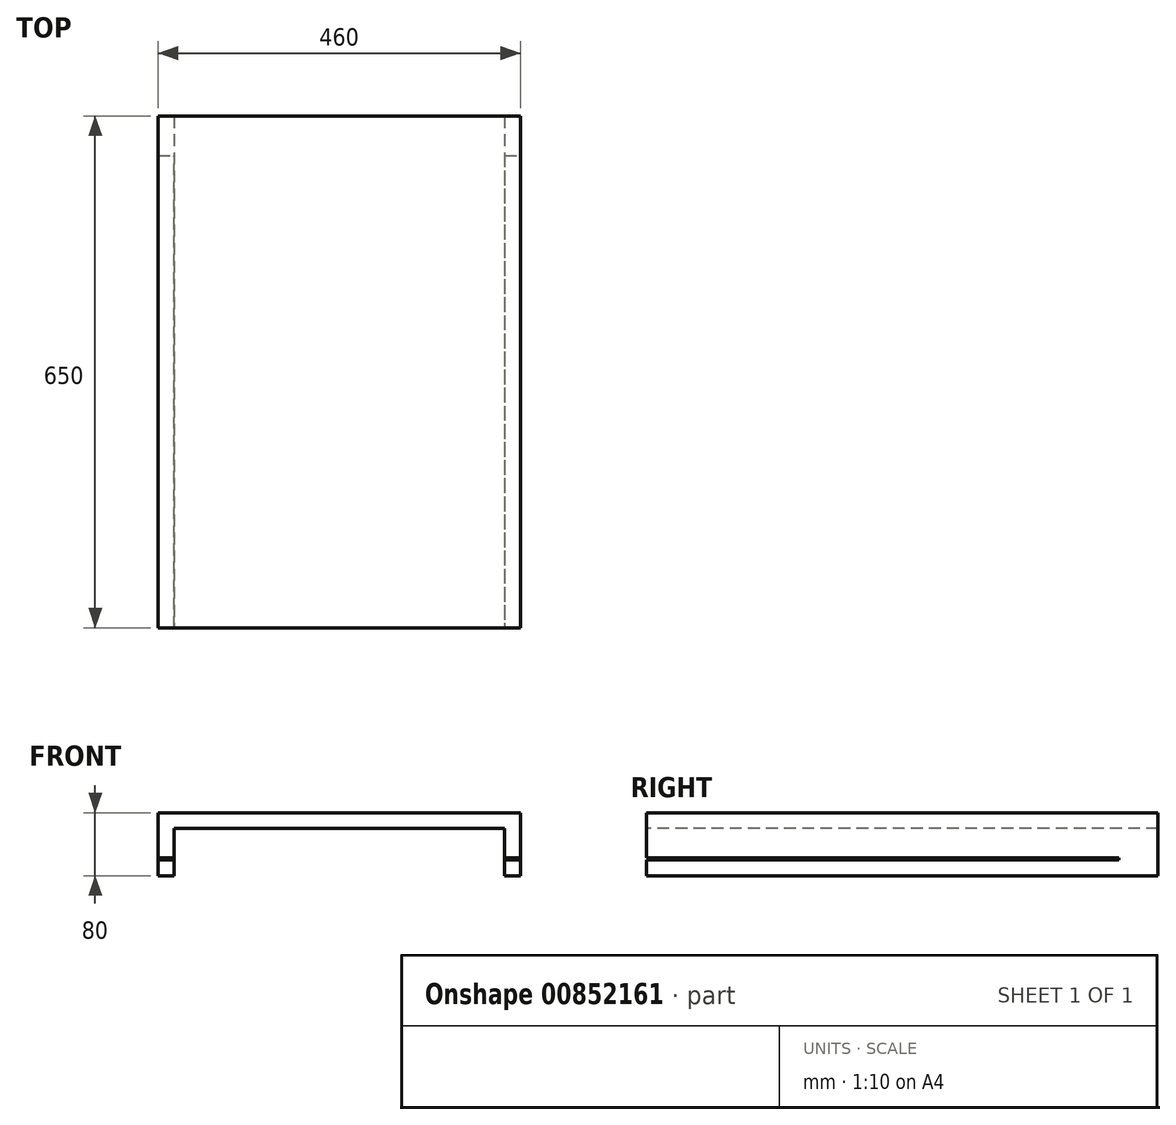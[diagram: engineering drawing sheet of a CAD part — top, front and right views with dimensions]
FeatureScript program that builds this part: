
annotation { "Feature Type Name" : "Feature", "Feature Type Description" : "" }
export const myFeature = defineFeature(function(context is Context, id is Id, definition is map)
    precondition{}
    {
        {
            var Q0;
            Q0=qCreatedBy(makeId("Top.planeOp"),FACE);
            var sketch = newSketch(context, id + "F0", { "sketchPlane" : qUnion([Q0])});
            skLineSegment(sketch, "E0.bottom", {"start": v(230, -325) * mm, "end": v(-230, -325) * mm});
            skLineSegment(sketch, "E0.top", {"start": v(230, 325) * mm, "end": v(-230, 325) * mm});
            skLineSegment(sketch, "E0.left", {"start": v(230, -325) * mm, "end": v(230, 325) * mm});
            skLineSegment(sketch, "E0.right", {"start": v(-230, -325) * mm, "end": v(-230, 325) * mm});
            skPoint(sketch, "E0.middle", {"position": v(0, 0) * mm});
            skSolve(sketch);
        }
        {
            var Q0;
            Q0=makeQuery(id+"F0.imprint","IMPRINT",FACE,{"disambiguationData":[TD([[makeQuery(id+"F0.imprint","IMPRINT",EDGE,{"derivedFrom":sQuery(id+"F0.wireOp",EDGE,"E0.bottom")}),-1.0]])]});
            extrude(context, id + "F1", {"entities" : qUnion([Q0]), "depth" : 80 * mm, "offsetDistance" : 25 * mm});
        }
        {
            var Q0;
            Q0=makeQuery(id+"F1.opExtrude","SWEPT_FACE",FACE,{"disambiguationData":[OSD([sQuery(id+"F0.wireOp",EDGE,"E0.bottom")])]});
            var sketch = newSketch(context, id + "F2", { "sketchPlane" : qUnion([Q0])});
            skLineSegment(sketch, "E1", {"start": v(-210, 0) * mm, "end": v(-210, 60) * mm});
            skLineSegment(sketch, "E2", {"start": v(-210, 60) * mm, "end": v(210, 60) * mm});
            skLineSegment(sketch, "E3", {"start": v(210, 60) * mm, "end": v(210, 0) * mm});
            skSolve(sketch);
        }
        {
            var Q0;
            {var subQ0=sQuery(id+"F2.wireOp",EDGE,"E1");Q0=makeQuery(id+"F2.imprint","IMPRINT",FACE,{"disambiguationData":[TD([[makeQuery(id+"F2.imprint","IMPRINT",EDGE,{"derivedFrom":subQ0}),-1.0]])]});}
            var Q1;
            Q1=sQuery(id+"F2.wireOp",EDGE,"E2");
            var Q2;
            Q2=sQuery(id+"F2.wireOp",EDGE,"E3");
            var Q3;
            Q3=sQuery(id+"F2.wireOp",EDGE,"E1");
            extrude(context, id + "F3", {"entities" : qUnion([Q0]), "operationType" : NewBodyOperationType.REMOVE, "surfaceEntities" : qUnion([Q1, Q2, Q3]), "endBound" : BoundingType.THROUGH_ALL, "oppositeDirection" : true, "depth" : 25 * mm, "offsetDistance" : 25 * mm});
        }
        {
            var Q0;
            Q0=makeQuery(id+"F1.opExtrude","SWEPT_FACE",FACE,{"disambiguationData":[OSD([sQuery(id+"F0.wireOp",EDGE,"E0.left")])]});
            var sketch = newSketch(context, id + "F4", { "sketchPlane" : qUnion([Q0])});
            skLineSegment(sketch, "E4", {"start": v(-325, 22.5) * mm, "end": v(275, 22.5) * mm});
            skLineSegment(sketch, "E5", {"start": v(-325, 20) * mm, "end": v(275, 20) * mm});
            skLineSegment(sketch, "E6", {"start": v(275, 22.5) * mm, "end": v(275, 20) * mm});
            skSolve(sketch);
        }
        {
            var Q0;
            {var subQ0=sQuery(id+"F4.wireOp",EDGE,"E4");Q0=makeQuery(id+"F4.imprint","IMPRINT",FACE,{"disambiguationData":[TD([[makeQuery(id+"F4.imprint","IMPRINT",EDGE,{"derivedFrom":subQ0}),-1.0]])]});}
            extrude(context, id + "F5", {"entities" : qUnion([Q0]), "operationType" : NewBodyOperationType.REMOVE, "endBound" : BoundingType.THROUGH_ALL, "oppositeDirection" : true, "depth" : 25 * mm, "offsetDistance" : 25 * mm});
        }
    });
